# Revit family: GR_Адаптер линейный_Муфта(1)_VL-V-КСД_R21
name_source: partatom
category: Соединительные детали воздуховодов
units: mm (PartAtom-declared; Revit-internal decimal feet)

## family parameters
Всегда вертикально = Да
Заголовок OmniClass = Metal Ducts
На основе рабочей плоскости = Нет
Номер OmniClass = 23.75.70.14.31
Общий = Нет
При загрузке вырезать с полостями = Нет
Размер круглого соединителя = Использовать диаметр
Тип детали = Мультипорт

## types (15) — shared parameters
ADSK_URL страницы изделия = https://grilles.ru
ADSK_Версия Revit = 2021
ADSK_Единица измерения = шт.
ADSK_Завод-изготовитель = ООО "ВЕНТРЕШЕТКИКОМ"
ADSK_Код изделия = 000157
ADSK_Количество = 1
ADSK_Материал = ADSK_Оцинкованная сталь
ADSK_Наименование = VL-V-КСД, адаптер вентиляционной решётки
Изготовитель = ООО "ВЕНТРЕШЕТКИКОМ"
Корпус_Металл_Толщина = 1 мм
Муфта_Металл_Толщина = 1 мм
zero-valued in all types: Отметка по умолчанию

## per-type parameters (varying)
| type | Корпус_Высота | Корпус_Длина | Решётка_Высота | Решётка_Положение_Центр |
| VL-V-КСД 1-20 | 182 мм | 86 мм | 46 мм | 43 мм |
| VL-V-КСД 1-30 | 182 мм | 96 мм | 56 мм | 48 мм |
| VL-V-КСД 1-40 | 222 мм | 106 мм | 66 мм | 53 мм |
| VL-V-КСД 1-50 | 222 мм | 116 мм | 76 мм | 58 мм |
| VL-V-КСД 1-60 | 272 мм | 126 мм | 86 мм | 63 мм |
| VL-V-КСД 1-70 | 272 мм | 136 мм | 96 мм | 68 мм |
| VL-V-КСД 2-20 | 222 мм | 126 мм | 86 мм | 63 мм |
| VL-V-КСД 2-25 | 222 мм | 136 мм | 96 мм | 68 мм |
| VL-V-КСД 2-30 | 222 мм | 146 мм | 106 мм | 73 мм |
| VL-V-КСД 3-20 | 222 мм | 166 мм | 126 мм | 83 мм |
| VL-V-КСД 3-25 | 222 мм | 181 мм | 141 мм | 91 мм |
| VL-V-КСД 3-30 | 222 мм | 196 мм | 156 мм | 98 мм |
| VL-V-КСД 4-20 | 272 мм | 206 мм | 166 мм | 103 мм |
| VL-V-КСД 4-25 | 272 мм | 226 мм | 186 мм | 113 мм |
| VL-V-КСД 4-30 | 272 мм | 246 мм | 206 мм | 123 мм |

note: column(s) folded — value = type name in every type: ADSK_Марка
